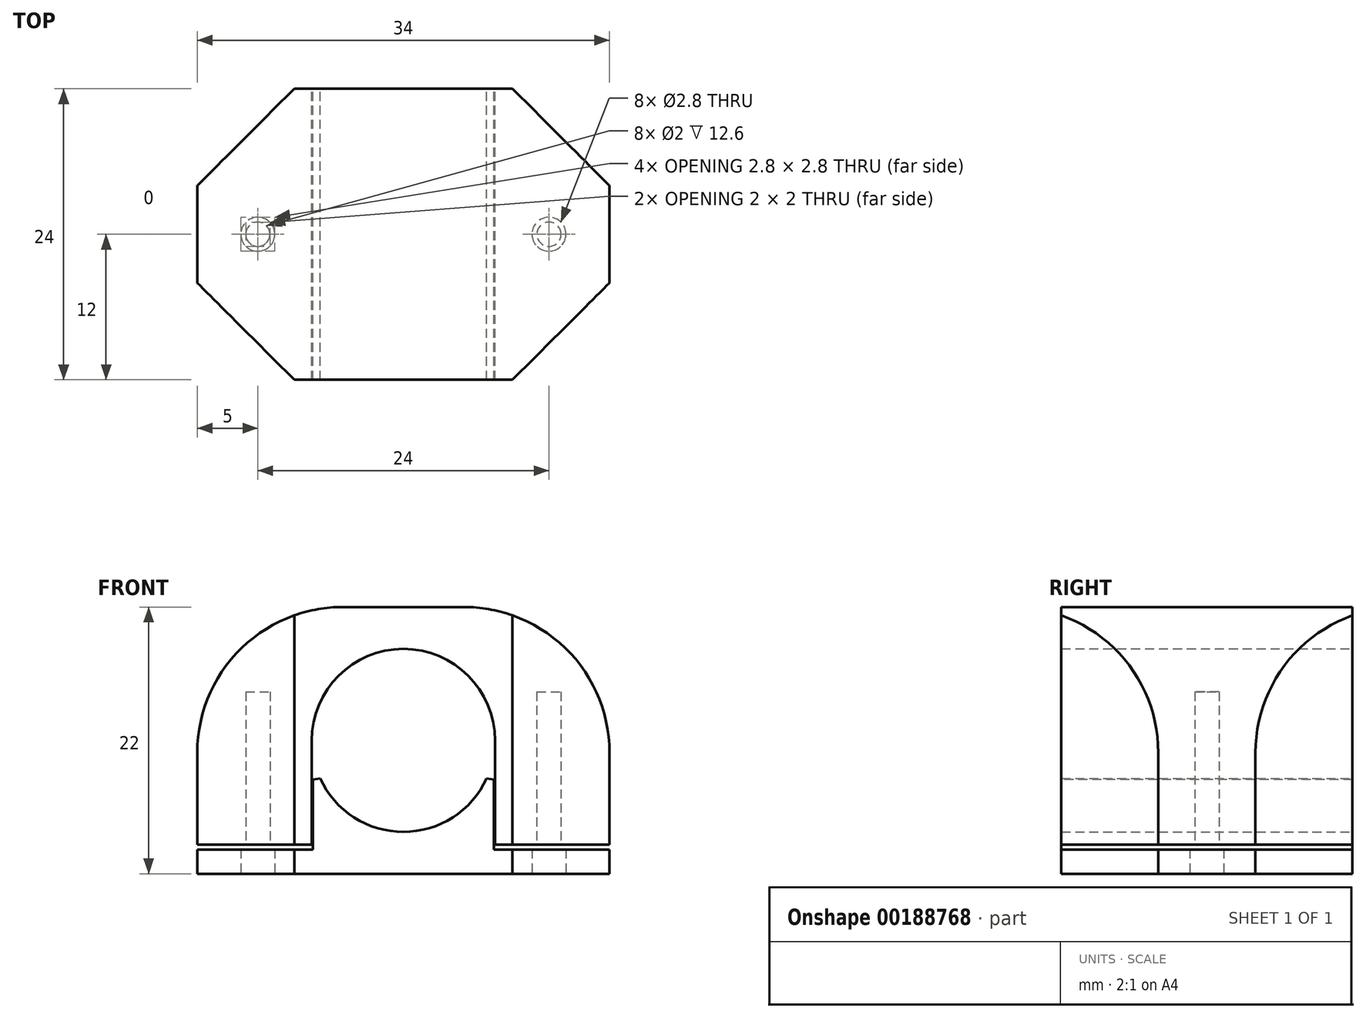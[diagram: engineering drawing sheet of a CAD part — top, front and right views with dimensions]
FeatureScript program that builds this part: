
annotation { "Feature Type Name" : "Feature", "Feature Type Description" : "" }
export const myFeature = defineFeature(function(context is Context, id is Id, definition is map)
    precondition{}
    {
        {
            var Q0;
            Q0=qCreatedBy(makeId("Front.planeOp"),FACE);
            var sketch = newSketch(context, id + "F0", { "sketchPlane" : qUnion([Q0])});
            skLineSegment(sketch, "E0.bottom", {"start": v(17, -11) * mm, "end": v(-17, -11) * mm});
            skLineSegment(sketch, "E0.top", {"start": v(5, 11) * mm, "end": v(-5, 11) * mm});
            skLineSegment(sketch, "E0.left", {"start": v(17, -11) * mm, "end": v(17, -1) * mm});
            skLineSegment(sketch, "E0.right", {"start": v(-17, -11) * mm, "end": v(-17, -1) * mm});
            skPoint(sketch, "E0.middle", {"position": v(0, 0) * mm});
            skCircle(sketch, "E1", {"center": v(0, 0) * mm, "radius": 7.55 * mm});
            skLineSegment(sketch, "E2", {"start": v(-17, -9) * mm, "end": v(17, -9) * mm});
            skLineSegment(sketch, "E3", {"start": v(-7.55, 0) * mm, "end": v(-7.55, -8.6) * mm});
            skLineSegment(sketch, "E4", {"start": v(7.55, 0) * mm, "end": v(7.55, -8.6) * mm});
            skLineSegment(sketch, "E5", {"start": v(-7.45, -9) * mm, "end": v(-7.45, -1.22) * mm});
            skLineSegment(sketch, "E6", {"start": v(7.45, -9) * mm, "end": v(7.45, -1.22) * mm});
            skLineSegment(sketch, "E7", {"start": v(-17, -8.6) * mm, "end": v(-7.55, -8.6) * mm});
            skLineSegment(sketch, "E8", {"start": v(17, -8.6) * mm, "end": v(7.55, -8.6) * mm});
            skPoint(sketch, "E9.visualSharp", {"position": v(-17, 11) * mm});
            skArc(sketch, "E9.filletArc", {"start": v(-5, 11) * mm, "mid": v(-13.49, 7.49) * mm, "end": v(-17, -1) * mm});
            skPoint(sketch, "E10.visualSharp", {"position": v(17, 11) * mm});
            skArc(sketch, "E10.filletArc", {"start": v(17, -1) * mm, "mid": v(13.49, 7.49) * mm, "end": v(5, 11) * mm});
            skSolve(sketch);
        }
        {
            var Q0;
            Q0=makeQuery(id+"F0.imprint","IMPRINT",FACE,{"disambiguationData":[TD([[makeQuery(id+"F0.imprint","IMPRINT",EDGE,{"derivedFrom":sQuery(id+"F0.wireOp",EDGE,"E0.top")}),1.0]])]});
            extrude(context, id + "F1", {"entities" : qUnion([Q0]), "depth" : 24 * mm, "offsetDistance" : 25 * mm});
        }
        {
            var Q0;
            {var subQ5=sQuery(id+"F0.wireOp",EDGE,"E0.bottom");Q0=makeQuery(id+"F0.imprint","IMPRINT",FACE,{"disambiguationData":[TD([[makeQuery(id+"F0.imprint","IMPRINT",EDGE,{"derivedFrom":subQ5}),-1.0]])]});}
            var Q1;
            {var subQ0=sQuery(id+"F0.wireOp",EDGE,"E5");Q1=makeQuery(id+"F0.imprint","IMPRINT",FACE,{"disambiguationData":[TD([[makeQuery(id+"F0.imprint","IMPRINT",EDGE,{"derivedFrom":subQ0}),-1.0]])]});}
            extrude(context, id + "F2", {"entities" : qUnion([Q0, Q1]), "depth" : 24 * mm, "offsetDistance" : 25 * mm});
        }
        {
            var Q0;
            Q0=makeQuery(id+"F2.opExtrude","SWEPT_FACE",FACE,{"disambiguationData":[OSD([sQuery(id+"F0.wireOp",EDGE,"E0.bottom")])]});
            var sketch = newSketch(context, id + "F3", { "sketchPlane" : qUnion([Q0])});
            skLineSegment(sketch, "E11", {"start": v(-9, 24) * mm, "end": v(-17, 16) * mm});
            skLineSegment(sketch, "E12", {"start": v(-9, 0) * mm, "end": v(-17, 8) * mm});
            skLineSegment(sketch, "E13", {"start": v(-17, 12) * mm, "end": v(17, 12) * mm, "construction": true});
            skLineSegment(sketch, "E14", {"start": v(9, 24) * mm, "end": v(17, 16) * mm});
            skLineSegment(sketch, "E15", {"start": v(9, 0) * mm, "end": v(17, 8) * mm});
            skLineSegment(sketch, "E16", {"start": v(0, 24) * mm, "end": v(0, 0) * mm, "construction": true});
            skSolve(sketch);
        }
        {
            var Q0;
            {var subQ0=sQuery(id+"F3.wireOp",EDGE,"E11");Q0=makeQuery(id+"F3.imprint","IMPRINT",FACE,{"disambiguationData":[TD([[makeQuery(id+"F3.imprint","IMPRINT",EDGE,{"derivedFrom":subQ0}),-1.0]])]});}
            var Q1;
            {var subQ0=sQuery(id+"F3.wireOp",EDGE,"E12");Q1=makeQuery(id+"F3.imprint","IMPRINT",FACE,{"disambiguationData":[TD([[makeQuery(id+"F3.imprint","IMPRINT",EDGE,{"derivedFrom":subQ0}),1.0]])]});}
            var Q2;
            {var subQ0=sQuery(id+"F3.wireOp",EDGE,"E15");Q2=makeQuery(id+"F3.imprint","IMPRINT",FACE,{"disambiguationData":[TD([[makeQuery(id+"F3.imprint","IMPRINT",EDGE,{"derivedFrom":subQ0}),-1.0]])]});}
            var Q3;
            {var subQ0=sQuery(id+"F3.wireOp",EDGE,"E14");Q3=makeQuery(id+"F3.imprint","IMPRINT",FACE,{"disambiguationData":[TD([[makeQuery(id+"F3.imprint","IMPRINT",EDGE,{"derivedFrom":subQ0}),1.0]])]});}
            extrude(context, id + "F4", {"entities" : qUnion([Q0, Q1, Q2, Q3]), "operationType" : NewBodyOperationType.REMOVE, "endBound" : BoundingType.THROUGH_ALL, "oppositeDirection" : true, "depth" : 25 * mm, "offsetDistance" : 25 * mm});
        }
        {
            var Q0;
            Q0=makeQuery(id+"F2.opExtrude","SWEPT_FACE",FACE,{"disambiguationData":[OSD([sQuery(id+"F0.wireOp",EDGE,"E0.bottom")])]});
            var sketch = newSketch(context, id + "F5", { "sketchPlane" : qUnion([Q0])});
            skLineSegment(sketch, "E17", {"start": v(-17, 12) * mm, "end": v(17, 12) * mm, "construction": true});
            skCircle(sketch, "E18", {"center": v(-12, 12) * mm, "radius": 1.4 * mm});
            skCircle(sketch, "E19", {"center": v(12, 12) * mm, "radius": 1.4 * mm});
            skLineSegment(sketch, "E20", {"start": v(0, 24) * mm, "end": v(0, 0) * mm, "construction": true});
            skCircle(sketch, "E21", {"center": v(-12, 12) * mm, "radius": 1 * mm});
            skCircle(sketch, "E22", {"center": v(12, 12) * mm, "radius": 1 * mm});
            skSolve(sketch);
        }
        {
            var Q0;
            Q0=makeQuery(id+"F5.imprint","IMPRINT",FACE,{"disambiguationData":[TD([[makeQuery(id+"F5.imprint","IMPRINT",EDGE,{"derivedFrom":sQuery(id+"F5.wireOp",EDGE,"E21")}),1.0]])]});
            var Q1;
            Q1=makeQuery(id+"F5.imprint","IMPRINT",FACE,{"disambiguationData":[TD([[makeQuery(id+"F5.imprint","IMPRINT",EDGE,{"derivedFrom":sQuery(id+"F5.wireOp",EDGE,"E22")}),1.0]])]});
            extrude(context, id + "F6", {"entities" : qUnion([Q0, Q1]), "operationType" : NewBodyOperationType.REMOVE, "oppositeDirection" : true, "depth" : 15 * mm, "offsetDistance" : 25 * mm});
        }
        {
            var Q0;
            Q0=makeQuery(id+"F5.imprint","IMPRINT",FACE,{"disambiguationData":[TD([[makeQuery(id+"F5.imprint","IMPRINT",EDGE,{"derivedFrom":sQuery(id+"F5.wireOp",EDGE,"E18")}),1.0]])]});
            var Q1;
            Q1=makeQuery(id+"F5.imprint","IMPRINT",FACE,{"disambiguationData":[TD([[makeQuery(id+"F5.imprint","IMPRINT",EDGE,{"derivedFrom":sQuery(id+"F5.wireOp",EDGE,"E19")}),1.0]])]});
            extrude(context, id + "F7", {"entities" : qUnion([Q0, Q1]), "operationType" : NewBodyOperationType.REMOVE, "endBound" : BoundingType.UP_TO_NEXT, "oppositeDirection" : true, "depth" : 25 * mm, "offsetDistance" : 25 * mm});
        }
        {
            var Q0;
            Q0=makeQuery(id+"F2.opExtrude","SWEPT_EDGE",EDGE,{"disambiguationData":[OSD([sQuery(id+"F0.wireOp",EDGE,"E1"),sQuery(id+"F0.wireOp",EDGE,"E5")])]});
            var Q1;
            Q1=makeQuery(id+"F2.opExtrude","SWEPT_EDGE",EDGE,{"disambiguationData":[OSD([sQuery(id+"F0.wireOp",EDGE,"E1"),sQuery(id+"F0.wireOp",EDGE,"E6")])]});
            chamfer(context, id + "F8", {"entities" : qUnion([Q0, Q1]), "width" : 2 * mm, "tangentPropagation" : true});
        }
    });
